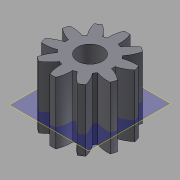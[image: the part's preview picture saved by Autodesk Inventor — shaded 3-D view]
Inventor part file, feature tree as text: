
AUTODESK INVENTOR PART (.ipt)
format: ipt  version: 2015 (Build 190159000, 159)  size: 166,912 bytes
history: native  units: in
note: dims shown in document units (in); Inventor stores cm internally (conversion verified against a paired STEP export)
features: other x13, sketch x3, plane x2
ambient origin geometry x8: Origin, YZ Plane, XZ Plane, XY Plane, X Axis, Y Axis, Z Axis, Center Point
bodies: Solid1 (feature_tree)
feature tree (18):
  other  "Spur Gear19_MIR3.ipt"
  other  "Solid1::Spur Gear19_MIR3.ipt"
  other  "TaggingFeature1"
  sketch  "Sketch1"  dims[d0=0.3937in]
  sketch  "Sketch2"  dims[d16=0.4724in d17=0.0in d41=0.0in d43=0.4724in d46=0.4724in d47=0.0in d48=0.0in]
  sketch  "Sketch3"
  plane  "XZ Plane_1"
  plane  "Work Plane2"
  other  "Z Axis_1"
  other  "Srf1"
  other  "Srf1::Derived"
  other  "Distance iMate"
  other  "Align iMate"
  other  "Mesh iMate"
  other  "Axis iMate"
  other  "Position iMate"
  other  "Mesh iMate2"
  other  "Start plane iMate"
